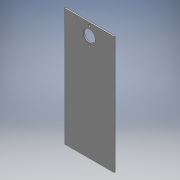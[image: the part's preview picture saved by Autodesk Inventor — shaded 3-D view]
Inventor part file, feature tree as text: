
AUTODESK INVENTOR PART (.ipt)
format: ipt  version: 2016 (Build 200138000, 138)  size: 103,936 bytes
history: native  units: mm
features: extrude x2, sketch x2, other x1
ambient origin geometry x8: Origin, YZ Plane, XZ Plane, XY Plane, X Axis, Y Axis, Z Axis, Center Point
bodies: Body1 (feature_tree)
feature tree (5):
  other  "ソリッド1"
  extrude  "押し出し1"  Depth=84.0mm
  extrude  "押し出し3"  Depth=200.0mm
  sketch  "スケッチ1"
  sketch  "スケッチ2"
